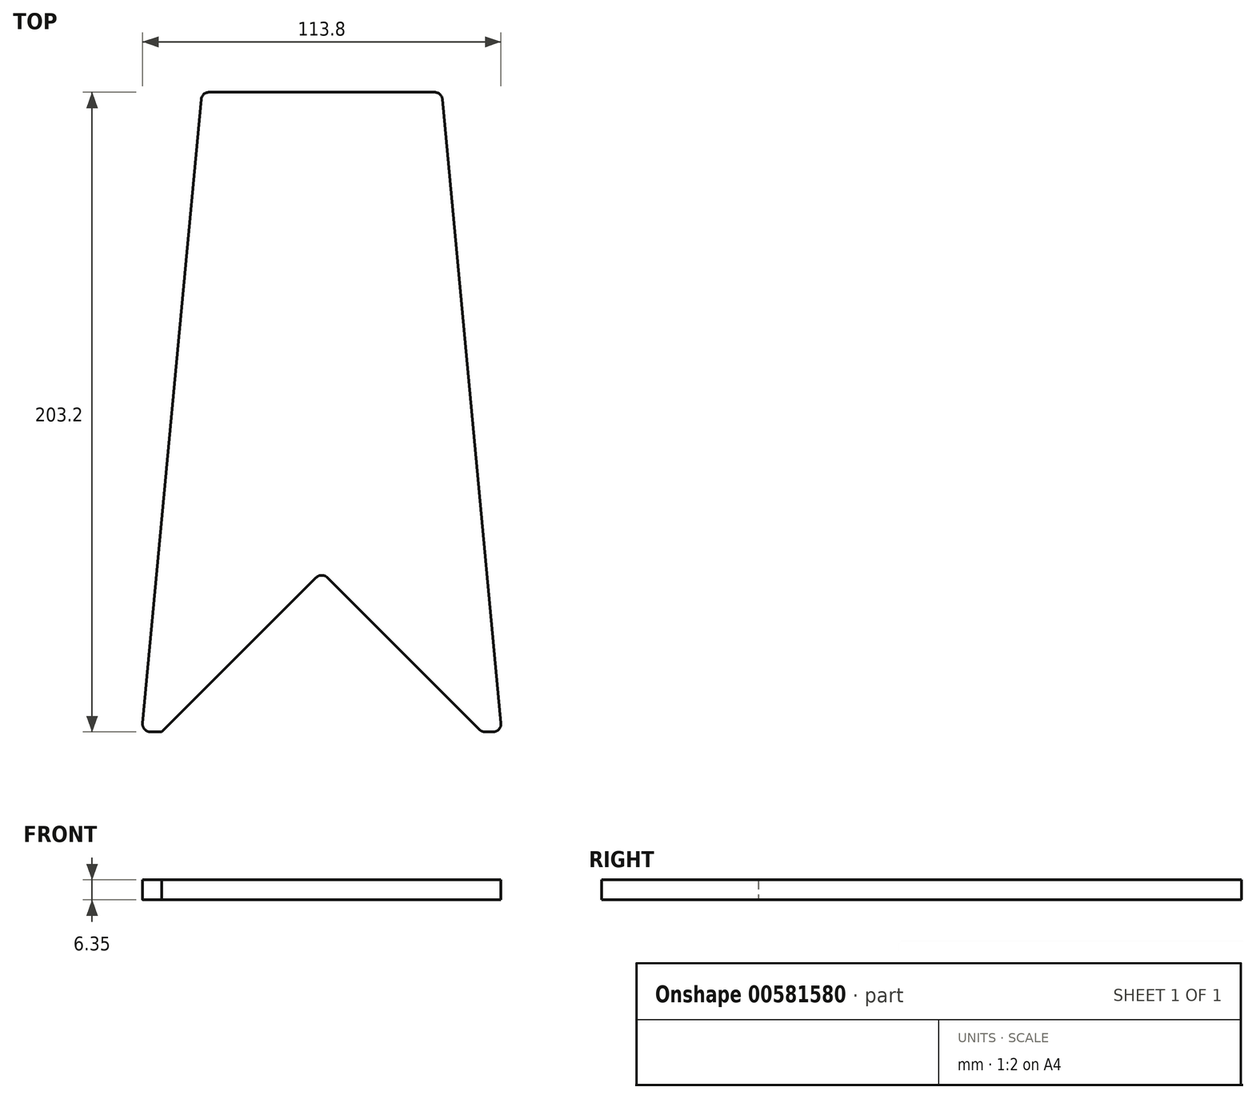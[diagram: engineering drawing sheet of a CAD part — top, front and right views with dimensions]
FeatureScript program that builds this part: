
annotation { "Feature Type Name" : "Feature", "Feature Type Description" : "" }
export const myFeature = defineFeature(function(context is Context, id is Id, definition is map)
    precondition{}
    {
        {
            var Q0;
            Q0=qCreatedBy(makeId("Top.planeOp"),FACE);
            var sketch = newSketch(context, id + "F0", { "sketchPlane" : qUnion([Q0])});
            skLineSegment(sketch, "E0", {"start": v(-57.15, 0) * mm, "end": v(57.15, 0) * mm});
            skLineSegment(sketch, "E1", {"start": v(57.15, 0) * mm, "end": v(38.1, 203.2) * mm});
            skLineSegment(sketch, "E2", {"start": v(38.1, 203.2) * mm, "end": v(-38.1, 203.2) * mm});
            skLineSegment(sketch, "E3", {"start": v(-38.1, 203.2) * mm, "end": v(-57.15, 0) * mm});
            skSolve(sketch);
        }
        {
            var Q0;
            Q0=makeQuery(id+"F0.imprint","IMPRINT",FACE,{"disambiguationData":[TD([[makeQuery(id+"F0.imprint","IMPRINT",EDGE,{"derivedFrom":sQuery(id+"F0.wireOp",EDGE,"E0")}),1.0]])]});
            extrude(context, id + "F1", {"entities" : qUnion([Q0]), "depth" : 6.35 * mm, "offsetDistance" : 25.4 * mm});
        }
        {
            var Q0;
            Q0=makeQuery(id+"F1.opExtrude","CAP_FACE",FACE,{"disambiguationData":[OSD([sQuery(id+"F0.wireOp",EDGE,"E0"),sQuery(id+"F0.wireOp",EDGE,"E1"),sQuery(id+"F0.wireOp",EDGE,"E2"),sQuery(id+"F0.wireOp",EDGE,"E3")])],"isStart":false});
            var sketch = newSketch(context, id + "F2", { "sketchPlane" : qUnion([Q0])});
            skLineSegment(sketch, "E4", {"start": v(-50.8, 0) * mm, "end": v(0, 50.8) * mm});
            skLineSegment(sketch, "E5", {"start": v(0, 50.8) * mm, "end": v(50.8, 0) * mm});
            skLineSegment(sketch, "E6", {"start": v(50.8, 0) * mm, "end": v(-50.8, 0) * mm});
            skSolve(sketch);
        }
        {
            var Q0;
            Q0=makeQuery(id+"F2.imprint","IMPRINT",FACE,{"disambiguationData":[TD([[makeQuery(id+"F2.imprint","IMPRINT",EDGE,{"derivedFrom":sQuery(id+"F2.wireOp",EDGE,"E4")}),-1.0]])]});
            extrude(context, id + "F3", {"entities" : qUnion([Q0]), "operationType" : NewBodyOperationType.REMOVE, "endBound" : BoundingType.THROUGH_ALL, "oppositeDirection" : true, "depth" : 25.4 * mm, "offsetDistance" : 25.4 * mm});
        }
        {
            var Q0;
            Q0=makeQuery(id+"F1.opExtrude","SWEPT_EDGE",EDGE,{"disambiguationData":[OSD([sQuery(id+"F0.wireOp",EDGE,"E2"),sQuery(id+"F0.wireOp",EDGE,"E3")])]});
            var Q1;
            Q1=makeQuery(id+"F1.opExtrude","SWEPT_EDGE",EDGE,{"disambiguationData":[OSD([sQuery(id+"F0.wireOp",EDGE,"E1"),sQuery(id+"F0.wireOp",EDGE,"E2")])]});
            var Q2;
            Q2=makeQuery(id+"F3.boolean.opBoolean","COPY",EDGE,{"derivedFrom":makeQuery(id+"F3.opExtrude","SWEPT_EDGE",EDGE,{"disambiguationData":[OSD([sQuery(id+"F2.wireOp",EDGE,"E4"),sQuery(id+"F2.wireOp",EDGE,"E5")])]})});
            var Q3;
            Q3=makeQuery(id+"F3.boolean.opBoolean","COPY",EDGE,{"derivedFrom":makeQuery(id+"F3.opExtrude","SWEPT_EDGE",EDGE,{"disambiguationData":[OSD([sQuery(id+"F0.wireOp",EDGE,"E0"),sQuery(id+"F2.wireOp",EDGE,"E4"),sQuery(id+"F2.wireOp",EDGE,"E6")])]})});
            var Q4;
            Q4=makeQuery(id+"F1.opExtrude","SWEPT_EDGE",EDGE,{"disambiguationData":[OSD([sQuery(id+"F0.wireOp",EDGE,"E0"),sQuery(id+"F0.wireOp",EDGE,"E3")])]});
            var Q5;
            Q5=makeQuery(id+"F3.boolean.opBoolean","COPY",EDGE,{"derivedFrom":makeQuery(id+"F3.opExtrude","SWEPT_EDGE",EDGE,{"disambiguationData":[OSD([sQuery(id+"F0.wireOp",EDGE,"E0"),sQuery(id+"F2.wireOp",EDGE,"E5"),sQuery(id+"F2.wireOp",EDGE,"E6")])]})});
            var Q6;
            Q6=makeQuery(id+"F1.opExtrude","SWEPT_EDGE",EDGE,{"disambiguationData":[OSD([sQuery(id+"F0.wireOp",EDGE,"E0"),sQuery(id+"F0.wireOp",EDGE,"E1")])]});
            fillet(context, id + "F4", {"entities" : qUnion([Q0, Q1, Q2, Q3, Q4, Q5, Q6]), "radius" : 2.54 * mm, "allowEdgeOverflow" : false});
        }
    });
